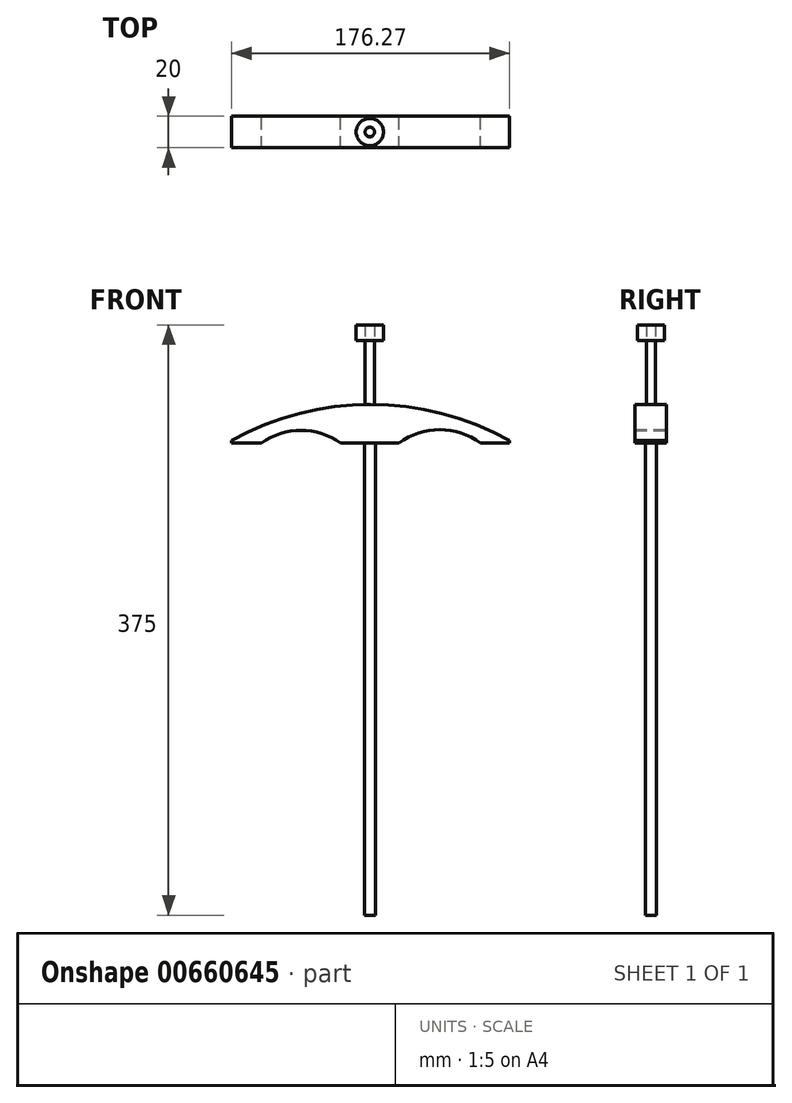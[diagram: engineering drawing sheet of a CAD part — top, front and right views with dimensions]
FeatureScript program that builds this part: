
annotation { "Feature Type Name" : "Feature", "Feature Type Description" : "" }
export const myFeature = defineFeature(function(context is Context, id is Id, definition is map)
    precondition{}
    {
        {
            var Q0;
            Q0=qCreatedBy(makeId("Front.planeOp"),FACE);
            var sketch = newSketch(context, id + "F0", { "sketchPlane" : qUnion([Q0])});
            skLineSegment(sketch, "E0", {"start": v(-97.83, 110.15) * mm, "end": v(-78.88, 110.15) * mm});
            skArc(sketch, "E1", {"start": v(78.44, 111.77) * mm, "mid": v(-9.7, 134.59) * mm, "end": v(-97.83, 111.77) * mm});
            skArc(sketch, "E2", {"start": v(-28.64, 110.15) * mm, "mid": v(-53.76, 118.1) * mm, "end": v(-78.88, 110.15) * mm});
            skPoint(sketch, "E2.centerSnap0", {"position": v(-53.76, 28.78) * mm});
            skPoint(sketch, "E3.centerSnap0", {"position": v(34.37, 28.78) * mm});
            skPoint(sketch, "E4.end.orphan", {"position": v(-97.83, 28.78) * mm});
            skLineSegment(sketch, "E5.trimOffspring", {"start": v(-28.64, 110.15) * mm, "end": v(8.42, 110.15) * mm});
            skLineSegment(sketch, "E6.trimOffspring", {"start": v(60.32, 110.15) * mm, "end": v(78.44, 110.15) * mm});
            skPoint(sketch, "E7.orphan", {"position": v(-9.7, 110.15) * mm});
            skArc(sketch, "E8.trimOffspring", {"start": v(60.32, 110.15) * mm, "mid": v(34.37, 118.59) * mm, "end": v(8.42, 110.15) * mm});
            skLineSegment(sketch, "E9", {"start": v(-97.83, 110.15) * mm, "end": v(-97.83, 111.77) * mm});
            skLineSegment(sketch, "E10", {"start": v(78.44, 110.15) * mm, "end": v(78.44, 111.77) * mm});
            skLineSegment(sketch, "E11", {"start": v(-9.7, 187.9) * mm, "end": v(-9.7, -162.1) * mm});
            skSolve(sketch);
        }
        {
            var Q0;
            Q0=makeQuery(id+"F0.imprint","IMPRINT",FACE,{"disambiguationData":[TD([[makeQuery(id+"F0.imprint","IMPRINT",EDGE,{"derivedFrom":sQuery(id+"F0.wireOp",EDGE,"E0")}),1.0]])]});
            var Q1;
            Q1=makeQuery(id+"F0.imprint","IMPRINT",FACE,{"disambiguationData":[TD([[makeQuery(id+"F0.imprint","IMPRINT",EDGE,{"derivedFrom":sQuery(id+"F0.wireOp",EDGE,"E6.trimOffspring")}),1.0]])]});
            extrude(context, id + "F1", {"entities" : qUnion([Q0, Q1]), "endBound" : BoundingType.SYMMETRIC, "depth" : 20 * mm, "offsetDistance" : 25 * mm});
        }
        {
            var Q0;
            Q0=makeQuery(id+"F1.opExtrude","SWEPT_FACE",FACE,{"disambiguationData":[OSD([sQuery(id+"F0.wireOp",EDGE,"E5.trimOffspring")])]});
            var sketch = newSketch(context, id + "F2", { "sketchPlane" : qUnion([Q0])});
            skLineSegment(sketch, "E12", {"start": v(-28.64, -10) * mm, "end": v(8.42, 10) * mm, "construction": true});
            skCircle(sketch, "E13", {"center": v(-10.11, 0) * mm, "radius": 3 * mm});
            skSolve(sketch);
        }
        {
            var Q0;
            Q0=makeQuery(id+"F2.imprint","IMPRINT",FACE,{"disambiguationData":[TD([[makeQuery(id+"F2.imprint","IMPRINT",EDGE,{"derivedFrom":sQuery(id+"F2.wireOp",EDGE,"E13")}),1.0]])]});
            extrude(context, id + "F3", {"entities" : qUnion([Q0]), "operationType" : NewBodyOperationType.ADD, "oppositeDirection" : true, "depth" : 75 * mm, "offsetDistance" : 25 * mm});
        }
        {
            var Q0;
            Q0=makeQuery(id+"F1.opExtrude","SWEPT_FACE",FACE,{"disambiguationData":[OSD([sQuery(id+"F0.wireOp",EDGE,"E5.trimOffspring")])]});
            var sketch = newSketch(context, id + "F4", { "sketchPlane" : qUnion([Q0])});
            skCircle(sketch, "E14", {"center": v(-10.11, 0) * mm, "radius": 3.5 * mm});
            skPoint(sketch, "E14.centerSnap0", {"position": v(-28.64, 0) * mm});
            skPoint(sketch, "E14.centerSnap1", {"position": v(-10.11, 10) * mm});
            skSolve(sketch);
        }
        {
            var Q0;
            Q0=makeQuery(id+"F4.imprint","IMPRINT",FACE,{"disambiguationData":[TD([[makeQuery(id+"F4.imprint","IMPRINT",EDGE,{"derivedFrom":sQuery(id+"F4.wireOp",EDGE,"E14")}),1.0]])]});
            extrude(context, id + "F5", {"entities" : qUnion([Q0]), "depth" : 300 * mm, "offsetDistance" : 25 * mm});
        }
        {
            var Q0;
            Q0=makeQuery(id+"F3.opExtrude","CAP_FACE",FACE,{"disambiguationData":[OSD([sQuery(id+"F2.wireOp",EDGE,"E13")])],"isStart":false});
            var sketch = newSketch(context, id + "F6", { "sketchPlane" : qUnion([Q0])});
            skCircle(sketch, "E15", {"center": v(-10.11, 0) * mm, "radius": 8.65 * mm});
            skSolve(sketch);
        }
        {
            var Q0;
            Q0 = qSketchRegion(id + "F6", true);
            extrude(context, id + "F7", {"entities" : qUnion([Q0]), "oppositeDirection" : true, "depth" : 10 * mm, "offsetDistance" : 25 * mm});
        }
    });
